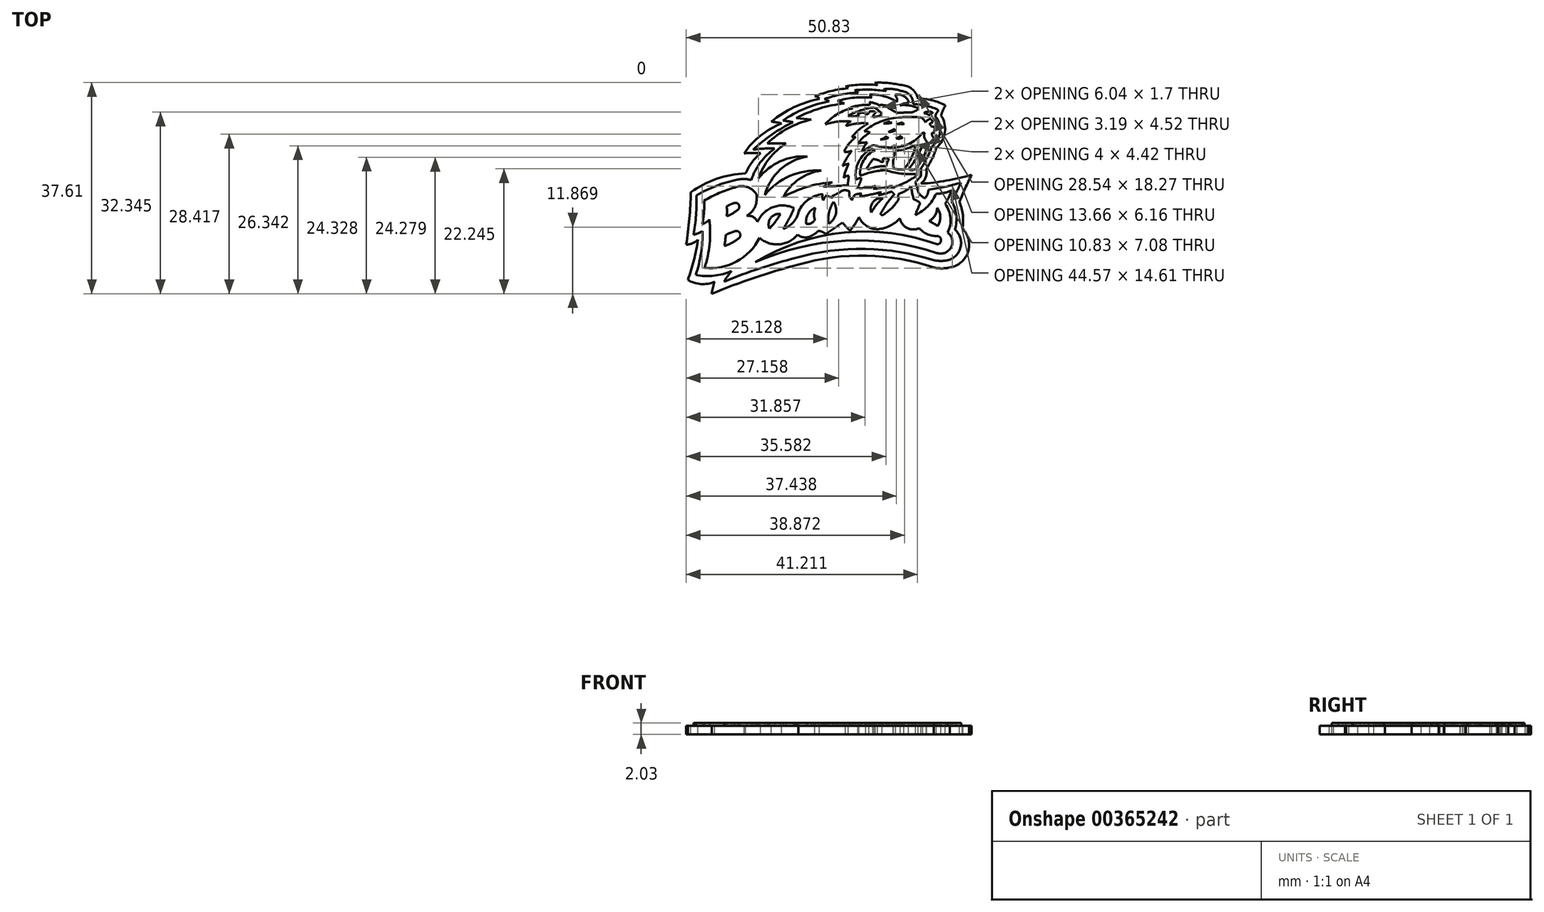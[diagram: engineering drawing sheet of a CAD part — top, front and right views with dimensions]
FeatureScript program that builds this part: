
annotation { "Feature Type Name" : "Feature", "Feature Type Description" : "" }
export const myFeature = defineFeature(function(context is Context, id is Id, definition is map)
    precondition{}
    {
        {
            var Q0;
            Q0=qCreatedBy(makeId("Top.planeOp"),FACE);
            var sketch = newSketch(context, id + "F0", { "sketchPlane" : qUnion([Q0])});
            skLineSegment(sketch, "E0", {"start": v(-9.68, 4.6) * mm, "end": v(-12.98, 4.6) * mm});
            skLineSegment(sketch, "E1", {"start": v(-7.81, 9.13) * mm, "end": v(-5.14, 8.87) * mm});
            skLineSegment(sketch, "E2", {"start": v(-0.46, 12.2) * mm, "end": v(0.77, 11.72) * mm});
            skLineSegment(sketch, "E3", {"start": v(5.28, 13.32) * mm, "end": v(5.62, 12.76) * mm});
            skArc(sketch, "E4", {"start": v(10.1, 12.03) * mm, "mid": v(7.78, 13.04) * mm, "end": v(5.28, 13.32) * mm});
            skArc(sketch, "E5", {"start": v(5.62, 12.76) * mm, "mid": v(2.55, 12.78) * mm, "end": v(-0.46, 12.2) * mm});
            skArc(sketch, "E6", {"start": v(0.77, 11.72) * mm, "mid": v(-3.65, 10.85) * mm, "end": v(-7.81, 9.13) * mm});
            skArc(sketch, "E7", {"start": v(-5.14, 8.87) * mm, "mid": v(-9.36, 7.3) * mm, "end": v(-12.98, 4.6) * mm});
            skArc(sketch, "E8", {"start": v(-9.68, 4.6) * mm, "mid": v(-12.64, 1.92) * mm, "end": v(-14.53, -1.6) * mm});
            skArc(sketch, "E9", {"start": v(-5.85, 2.3) * mm, "mid": v(-10.68, 1.43) * mm, "end": v(-14.53, -1.6) * mm});
            skArc(sketch, "E10", {"start": v(-5.85, 2.3) * mm, "mid": v(-10.66, -0.03) * mm, "end": v(-13.45, -4.58) * mm});
            skArc(sketch, "E11", {"start": v(-3.37, -0.22) * mm, "mid": v(-8.94, -1.17) * mm, "end": v(-13.45, -4.58) * mm});
            skArc(sketch, "E12", {"start": v(-3.37, -0.22) * mm, "mid": v(-7.34, -1.75) * mm, "end": v(-10.14, -4.94) * mm});
            skArc(sketch, "E13", {"start": v(-1.42, -2.32) * mm, "mid": v(-5.93, -3.13) * mm, "end": v(-10.14, -4.94) * mm});
            skArc(sketch, "E14", {"start": v(-1.42, -2.32) * mm, "mid": v(-2.2, -2.67) * mm, "end": v(-2.98, -3.05) * mm});
            skArc(sketch, "E15", {"start": v(-2.98, -3.05) * mm, "mid": v(-0.82, -2.97) * mm, "end": v(1.35, -2.86) * mm});
            skArc(sketch, "E16", {"start": v(1.55, -1.16) * mm, "mid": v(1.44, -2) * mm, "end": v(1.35, -2.86) * mm});
            skArc(sketch, "E17", {"start": v(1.55, -1.16) * mm, "mid": v(1.07, -1.21) * mm, "end": v(0.68, -1.5) * mm});
            skArc(sketch, "E18", {"start": v(1.55, 1.01) * mm, "mid": v(0.98, -0.2) * mm, "end": v(0.68, -1.5) * mm});
            skArc(sketch, "E19", {"start": v(1.55, 1.01) * mm, "mid": v(0.97, 0.86) * mm, "end": v(0.44, 0.6) * mm});
            skArc(sketch, "E20", {"start": v(2.1, 3.35) * mm, "mid": v(1.2, 2.02) * mm, "end": v(0.44, 0.6) * mm});
            skArc(sketch, "E21", {"start": v(0.68, 3.16) * mm, "mid": v(1.4, 3.13) * mm, "end": v(2.1, 3.35) * mm});
            skArc(sketch, "E22", {"start": v(2.8, 5.75) * mm, "mid": v(1.6, 4.58) * mm, "end": v(0.68, 3.16) * mm});
            skArc(sketch, "E23", {"start": v(2.8, 5.75) * mm, "mid": v(2.45, 5.77) * mm, "end": v(2.1, 5.75) * mm});
            skArc(sketch, "E24", {"start": v(4.98, 8.2) * mm, "mid": v(3.41, 7.12) * mm, "end": v(2.1, 5.75) * mm});
            skArc(sketch, "E25", {"start": v(4.98, 8.2) * mm, "mid": v(3, 8.16) * mm, "end": v(1.05, 7.73) * mm});
            skArc(sketch, "E26", {"start": v(1.94, 8.53) * mm, "mid": v(1.4, 8.23) * mm, "end": v(1.05, 7.73) * mm});
            skArc(sketch, "E27", {"start": v(1.94, 8.53) * mm, "mid": v(-0.37, 8.53) * mm, "end": v(-2.64, 8.02) * mm});
            skArc(sketch, "E28", {"start": v(2.29, 10.88) * mm, "mid": v(-0.43, 9.9) * mm, "end": v(-2.64, 8.02) * mm});
            skArc(sketch, "E29", {"start": v(2.29, 10.88) * mm, "mid": v(2.09, 10.98) * mm, "end": v(1.88, 11.07) * mm});
            skArc(sketch, "E30", {"start": v(5.25, 11.51) * mm, "mid": v(3.55, 11.41) * mm, "end": v(1.88, 11.07) * mm});
            skArc(sketch, "E31", {"start": v(5.25, 11.51) * mm, "mid": v(5.3, 11.75) * mm, "end": v(5.25, 11.98) * mm});
            skArc(sketch, "E32", {"start": v(6.95, 11.43) * mm, "mid": v(6.13, 11.8) * mm, "end": v(5.25, 11.98) * mm});
            skArc(sketch, "E33", {"start": v(8.33, 11.35) * mm, "mid": v(7.64, 11.45) * mm, "end": v(6.95, 11.43) * mm});
            skArc(sketch, "E34", {"start": v(8.55, 10.96) * mm, "mid": v(8.5, 11.2) * mm, "end": v(8.33, 11.35) * mm});
            skArc(sketch, "E35", {"start": v(8.55, 10.96) * mm, "mid": v(9.41, 10.45) * mm, "end": v(10.33, 10.05) * mm});
            skArc(sketch, "E36", {"start": v(12.82, 10.15) * mm, "mid": v(11.58, 10.13) * mm, "end": v(10.33, 10.05) * mm});
            skArc(sketch, "E37", {"start": v(12.82, 10.15) * mm, "mid": v(13.46, 10.44) * mm, "end": v(14, 10.88) * mm});
            skArc(sketch, "E38", {"start": v(14, 10.88) * mm, "mid": v(12.37, 11.37) * mm, "end": v(10.67, 11.43) * mm});
            skArc(sketch, "E39", {"start": v(12.27, 11.86) * mm, "mid": v(11.45, 11.74) * mm, "end": v(10.67, 11.43) * mm});
            skArc(sketch, "E40", {"start": v(10.1, 12.03) * mm, "mid": v(10.1, 12.7) * mm, "end": v(9.75, 13.25) * mm});
            skArc(sketch, "E41", {"start": v(12.27, 11.86) * mm, "mid": v(11.3, 13.08) * mm, "end": v(9.75, 13.25) * mm});
            skArc(sketch, "E42", {"start": v(16.51, 10.14) * mm, "mid": v(15.71, 10.28) * mm, "end": v(14.93, 10.05) * mm});
            skArc(sketch, "E43", {"start": v(16.17, 9.93) * mm, "mid": v(16.36, 10) * mm, "end": v(16.51, 10.14) * mm});
            skArc(sketch, "E44", {"start": v(15.52, 9.9) * mm, "mid": v(15.85, 9.7) * mm, "end": v(16.17, 9.93) * mm});
            skArc(sketch, "E45", {"start": v(14.93, 10.05) * mm, "mid": v(15.22, 9.95) * mm, "end": v(15.52, 9.9) * mm});
            skArc(sketch, "E46", {"start": v(6.07, 11.05) * mm, "mid": v(3.67, 10.5) * mm, "end": v(1.42, 9.55) * mm});
            skArc(sketch, "E47", {"start": v(7.46, 9.83) * mm, "mid": v(6.81, 10.5) * mm, "end": v(6.07, 11.05) * mm});
            skArc(sketch, "E48", {"start": v(5.83, 9.35) * mm, "mid": v(6.7, 9.44) * mm, "end": v(7.46, 9.83) * mm});
            skArc(sketch, "E49", {"start": v(6.3, 10.05) * mm, "mid": v(6, 9.74) * mm, "end": v(5.83, 9.35) * mm});
            skArc(sketch, "E50", {"start": v(6.3, 10.05) * mm, "mid": v(6.26, 10.17) * mm, "end": v(6.18, 10.26) * mm});
            skArc(sketch, "E51", {"start": v(6.18, 10.26) * mm, "mid": v(5.66, 10.36) * mm, "end": v(5.14, 10.26) * mm});
            skArc(sketch, "E52", {"start": v(4.58, 9.85) * mm, "mid": v(4.98, 9.89) * mm, "end": v(5.14, 10.26) * mm});
            skArc(sketch, "E53", {"start": v(4.58, 9.85) * mm, "mid": v(4.31, 10.05) * mm, "end": v(3.98, 10.11) * mm});
            skArc(sketch, "E54", {"start": v(3.98, 10.11) * mm, "mid": v(3.54, 10.03) * mm, "end": v(3.14, 9.85) * mm});
            skArc(sketch, "E55", {"start": v(3.35, 9.58) * mm, "mid": v(3.26, 9.72) * mm, "end": v(3.14, 9.85) * mm});
            skArc(sketch, "E56", {"start": v(1.42, 9.55) * mm, "mid": v(2.38, 9.47) * mm, "end": v(3.35, 9.58) * mm});
            skArc(sketch, "E57", {"start": v(10.38, 9.25) * mm, "mid": v(7.14, 8.5) * mm, "end": v(4.28, 6.8) * mm});
            skArc(sketch, "E58", {"start": v(14.46, 9.25) * mm, "mid": v(12.42, 9.35) * mm, "end": v(10.38, 9.25) * mm});
            skArc(sketch, "E59", {"start": v(15.21, 8.4) * mm, "mid": v(14.88, 8.86) * mm, "end": v(14.46, 9.25) * mm});
            skArc(sketch, "E60", {"start": v(16.06, 9.01) * mm, "mid": v(15.59, 8.77) * mm, "end": v(15.21, 8.4) * mm});
            skArc(sketch, "E61", {"start": v(16.54, 8.4) * mm, "mid": v(16.35, 8.74) * mm, "end": v(16.06, 9.01) * mm});
            skArc(sketch, "E62", {"start": v(16.54, 8.4) * mm, "mid": v(16.21, 8.27) * mm, "end": v(15.92, 8.08) * mm});
            skArc(sketch, "E63", {"start": v(16.29, 7.63) * mm, "mid": v(16.12, 7.87) * mm, "end": v(15.92, 8.08) * mm});
            skArc(sketch, "E64", {"start": v(16.8, 7.55) * mm, "mid": v(16.55, 7.62) * mm, "end": v(16.29, 7.63) * mm});
            skArc(sketch, "E65", {"start": v(16.71, 6.51) * mm, "mid": v(16.84, 7.03) * mm, "end": v(16.8, 7.55) * mm});
            skArc(sketch, "E66", {"start": v(16.38, 6.52) * mm, "mid": v(16.55, 6.5) * mm, "end": v(16.71, 6.51) * mm});
            skArc(sketch, "E67", {"start": v(16.38, 6.52) * mm, "mid": v(16.39, 6.2) * mm, "end": v(16.43, 5.9) * mm});
            skArc(sketch, "E68", {"start": v(16.8, 5.4) * mm, "mid": v(16.65, 5.68) * mm, "end": v(16.43, 5.9) * mm});
            skArc(sketch, "E69", {"start": v(15.82, 4.56) * mm, "mid": v(16.37, 4.92) * mm, "end": v(16.8, 5.4) * mm});
            skArc(sketch, "E70", {"start": v(14.95, 6.1) * mm, "mid": v(15.2, 5.23) * mm, "end": v(15.82, 4.56) * mm});
            skArc(sketch, "E71", {"start": v(15.03, 6.33) * mm, "mid": v(14.95, 6.24) * mm, "end": v(14.95, 6.1) * mm});
            skArc(sketch, "E72", {"start": v(15.03, 6.33) * mm, "mid": v(15.02, 6.48) * mm, "end": v(14.88, 6.51) * mm});
            skArc(sketch, "E73", {"start": v(14.88, 6.51) * mm, "mid": v(14.73, 6.48) * mm, "end": v(14.61, 6.38) * mm});
            skArc(sketch, "E74", {"start": v(9.25, 3.89) * mm, "mid": v(12.22, 4.51) * mm, "end": v(14.61, 6.38) * mm});
            skArc(sketch, "E75", {"start": v(5.98, 4.3) * mm, "mid": v(7.6, 3.98) * mm, "end": v(9.25, 3.89) * mm});
            skArc(sketch, "E76", {"start": v(5.98, 4.3) * mm, "mid": v(5.63, 4.2) * mm, "end": v(5.3, 4.04) * mm});
            skArc(sketch, "E77", {"start": v(3.85, 3.19) * mm, "mid": v(4.59, 3.6) * mm, "end": v(5.3, 4.04) * mm});
            skArc(sketch, "E78", {"start": v(4.81, 4.79) * mm, "mid": v(4.27, 4.02) * mm, "end": v(3.85, 3.19) * mm});
            skArc(sketch, "E79", {"start": v(4.81, 4.79) * mm, "mid": v(4, 4.75) * mm, "end": v(3.19, 4.62) * mm});
            skArc(sketch, "E80", {"start": v(5.3, 6.55) * mm, "mid": v(4.13, 5.7) * mm, "end": v(3.19, 4.62) * mm});
            skArc(sketch, "E81", {"start": v(5.3, 6.55) * mm, "mid": v(4.81, 6.76) * mm, "end": v(4.28, 6.8) * mm});
            skArc(sketch, "E82", {"start": v(7.73, 8.16) * mm, "mid": v(8.25, 8.34) * mm, "end": v(8.74, 8.56) * mm});
            skArc(sketch, "E83", {"start": v(8.74, 8.56) * mm, "mid": v(8.94, 8.35) * mm, "end": v(9.23, 8.31) * mm});
            skArc(sketch, "E84", {"start": v(7.73, 8.16) * mm, "mid": v(8.49, 8.18) * mm, "end": v(9.23, 8.31) * mm});
            skArc(sketch, "E85", {"start": v(10.14, 8.12) * mm, "mid": v(10.6, 8.2) * mm, "end": v(11.03, 8.42) * mm});
            skArc(sketch, "E86", {"start": v(11.03, 8.42) * mm, "mid": v(11.18, 8.22) * mm, "end": v(11.42, 8.12) * mm});
            skArc(sketch, "E87", {"start": v(10.14, 8.12) * mm, "mid": v(10.78, 8.02) * mm, "end": v(11.42, 8.12) * mm});
            skArc(sketch, "E88", {"start": v(7.17, 5.33) * mm, "mid": v(7.9, 5.4) * mm, "end": v(8.6, 5.6) * mm});
            skArc(sketch, "E89", {"start": v(8.17, 5.86) * mm, "mid": v(8.38, 5.72) * mm, "end": v(8.6, 5.6) * mm});
            skArc(sketch, "E90", {"start": v(7.17, 5.33) * mm, "mid": v(7.72, 5.51) * mm, "end": v(8.17, 5.86) * mm});
            skArc(sketch, "E91", {"start": v(9.96, 5.53) * mm, "mid": v(10.4, 5.7) * mm, "end": v(10.77, 5.98) * mm});
            skArc(sketch, "E92", {"start": v(10.77, 5.98) * mm, "mid": v(10.9, 5.75) * mm, "end": v(11.15, 5.66) * mm});
            skArc(sketch, "E93", {"start": v(9.96, 5.53) * mm, "mid": v(10.57, 5.48) * mm, "end": v(11.15, 5.66) * mm});
            skArc(sketch, "E94", {"start": v(8.6, 6.68) * mm, "mid": v(9.14, 6.93) * mm, "end": v(9.65, 7.2) * mm});
            skArc(sketch, "E95", {"start": v(9.65, 7.2) * mm, "mid": v(9.74, 7.05) * mm, "end": v(9.88, 6.95) * mm});
            skArc(sketch, "E96", {"start": v(8.6, 6.68) * mm, "mid": v(9.26, 6.73) * mm, "end": v(9.88, 6.95) * mm});
            skArc(sketch, "E97", {"start": v(5.52, 3.63) * mm, "mid": v(3.3, 1.34) * mm, "end": v(2.8, -1.81) * mm});
            skArc(sketch, "E98", {"start": v(3.7, -1.49) * mm, "mid": v(3.25, -1.64) * mm, "end": v(2.8, -1.81) * mm});
            skArc(sketch, "E99", {"start": v(3.64, -2.08) * mm, "mid": v(3.72, -1.79) * mm, "end": v(3.7, -1.49) * mm});
            skArc(sketch, "E100", {"start": v(3.08, -3.32) * mm, "mid": v(3.39, -2.71) * mm, "end": v(3.64, -2.08) * mm});
            skArc(sketch, "E101", {"start": v(3.08, -3.32) * mm, "mid": v(4.74, -3.29) * mm, "end": v(6.35, -2.9) * mm});
            skArc(sketch, "E102", {"start": v(5.9, -3.45) * mm, "mid": v(6.2, -3.23) * mm, "end": v(6.35, -2.9) * mm});
            skArc(sketch, "E103", {"start": v(5.9, -3.45) * mm, "mid": v(7.63, -3.3) * mm, "end": v(9.31, -2.9) * mm});
            skArc(sketch, "E104", {"start": v(9.1, -3.27) * mm, "mid": v(9.24, -3.1) * mm, "end": v(9.31, -2.9) * mm});
            skArc(sketch, "E105", {"start": v(9.1, -3.27) * mm, "mid": v(11.43, -2.43) * mm, "end": v(13.54, -1.16) * mm});
            skArc(sketch, "E106", {"start": v(13.54, -1.16) * mm, "mid": v(13.58, -1) * mm, "end": v(13.54, -0.84) * mm});
            skArc(sketch, "E107", {"start": v(8.15, -0.14) * mm, "mid": v(10.81, -0.75) * mm, "end": v(13.54, -0.84) * mm});
            skArc(sketch, "E108", {"start": v(8.15, -0.14) * mm, "mid": v(5.82, -0.44) * mm, "end": v(3.58, -1.16) * mm});
            skArc(sketch, "E109", {"start": v(6.23, 3.41) * mm, "mid": v(4.15, 1.56) * mm, "end": v(3.58, -1.16) * mm});
            skArc(sketch, "E110", {"start": v(6.23, 3.41) * mm, "mid": v(5.89, 3.57) * mm, "end": v(5.52, 3.63) * mm});
            skArc(sketch, "E111", {"start": v(4.7, 0.16) * mm, "mid": v(5.28, 0.98) * mm, "end": v(5.8, 1.83) * mm});
            skArc(sketch, "E112", {"start": v(4.93, 0) * mm, "mid": v(4.86, 0.15) * mm, "end": v(4.7, 0.16) * mm});
            skArc(sketch, "E113", {"start": v(8.24, 0.59) * mm, "mid": v(6.56, 0.46) * mm, "end": v(4.93, 0) * mm});
            skArc(sketch, "E114", {"start": v(8.6, 1.67) * mm, "mid": v(8.37, 1.15) * mm, "end": v(8.24, 0.59) * mm});
            skArc(sketch, "E115", {"start": v(8.6, 1.67) * mm, "mid": v(8.6, 1.81) * mm, "end": v(8.55, 1.94) * mm});
            skArc(sketch, "E116", {"start": v(8.55, 1.94) * mm, "mid": v(8.1, 1.96) * mm, "end": v(7.66, 1.92) * mm});
            skArc(sketch, "E117", {"start": v(7.66, 1.92) * mm, "mid": v(7.63, 1.7) * mm, "end": v(7.7, 1.47) * mm});
            skArc(sketch, "E118", {"start": v(7.33, 1.33) * mm, "mid": v(7.55, 1.31) * mm, "end": v(7.7, 1.47) * mm});
            skArc(sketch, "E119", {"start": v(7.33, 1.33) * mm, "mid": v(6.6, 1.7) * mm, "end": v(5.8, 1.83) * mm});
            skArc(sketch, "E120", {"start": v(9.88, 3.3) * mm, "mid": v(11.73, 3.65) * mm, "end": v(13.45, 4.39) * mm});
            skArc(sketch, "E121", {"start": v(11.33, 0) * mm, "mid": v(12.7, 2.04) * mm, "end": v(13.45, 4.39) * mm});
            skArc(sketch, "E122", {"start": v(9.52, 0.16) * mm, "mid": v(10.42, -0.02) * mm, "end": v(11.33, 0) * mm});
            skArc(sketch, "E123", {"start": v(9.88, 3.3) * mm, "mid": v(9.5, 1.76) * mm, "end": v(9.52, 0.16) * mm});
            skArc(sketch, "E124", {"start": v(12.2, 0) * mm, "mid": v(13.62, 2.1) * mm, "end": v(14.72, 4.39) * mm});
            skArc(sketch, "E125", {"start": v(15.39, 3.63) * mm, "mid": v(15.11, 4.06) * mm, "end": v(14.72, 4.39) * mm});
            skArc(sketch, "E126", {"start": v(13.45, 0.07) * mm, "mid": v(14.61, 1.75) * mm, "end": v(15.39, 3.63) * mm});
            skArc(sketch, "E127", {"start": v(12.2, 0) * mm, "mid": v(12.83, -0.13) * mm, "end": v(13.45, 0.07) * mm});
            skArc(sketch, "E128", {"start": v(13.02, 11.85) * mm, "mid": v(12.36, 13.32) * mm, "end": v(10.87, 13.95) * mm});
            skArc(sketch, "E129", {"start": v(10.87, 13.95) * mm, "mid": v(9.33, 14.32) * mm, "end": v(7.74, 14.28) * mm});
            skArc(sketch, "E130", {"start": v(8.16, 13.95) * mm, "mid": v(7.98, 14.16) * mm, "end": v(7.74, 14.28) * mm});
            skArc(sketch, "E131", {"start": v(8.16, 13.95) * mm, "mid": v(5.37, 14.2) * mm, "end": v(2.56, 14.1) * mm});
            skArc(sketch, "E132", {"start": v(3.2, 13.67) * mm, "mid": v(2.91, 13.93) * mm, "end": v(2.56, 14.1) * mm});
            skArc(sketch, "E133", {"start": v(3.2, 13.67) * mm, "mid": v(0.16, 13.34) * mm, "end": v(-2.78, 12.53) * mm});
            skArc(sketch, "E134", {"start": v(-1.98, 12.13) * mm, "mid": v(-2.37, 12.36) * mm, "end": v(-2.78, 12.53) * mm});
            skArc(sketch, "E135", {"start": v(-1.98, 12.13) * mm, "mid": v(-6.26, 10.84) * mm, "end": v(-10.2, 8.72) * mm});
            skArc(sketch, "E136", {"start": v(-8.38, 8.4) * mm, "mid": v(-9.3, 8.57) * mm, "end": v(-10.2, 8.72) * mm});
            skArc(sketch, "E137", {"start": v(-8.38, 8.4) * mm, "mid": v(-12.13, 6.22) * mm, "end": v(-15.5, 3.49) * mm});
            skArc(sketch, "E138", {"start": v(-11.68, 3.7) * mm, "mid": v(-13.6, 3.7) * mm, "end": v(-15.5, 3.49) * mm});
            skArc(sketch, "E139", {"start": v(-11.68, 3.7) * mm, "mid": v(-14.21, 1.23) * mm, "end": v(-15.86, -1.9) * mm});
            skArc(sketch, "E140", {"start": v(-24.58, -9.74) * mm, "mid": v(-24.27, -7.67) * mm, "end": v(-24.25, -5.57) * mm});
            skArc(sketch, "E141", {"start": v(-24.58, -9.74) * mm, "mid": v(-23.88, -9.42) * mm, "end": v(-23.3, -8.93) * mm});
            skArc(sketch, "E142", {"start": v(-24.17, -17.55) * mm, "mid": v(-23.26, -13.28) * mm, "end": v(-23.3, -8.93) * mm});
            skArc(sketch, "E143", {"start": v(-24.17, -17.55) * mm, "mid": v(-18.43, -16.4) * mm, "end": v(-14.35, -12.2) * mm});
            skArc(sketch, "E144", {"start": v(-14.35, -12.2) * mm, "mid": v(-10.86, -13.35) * mm, "end": v(-7.61, -11.64) * mm});
            skArc(sketch, "E145", {"start": v(-7.61, -11.64) * mm, "mid": v(-6.2, -12.12) * mm, "end": v(-4.78, -11.64) * mm});
            skArc(sketch, "E146", {"start": v(-4.78, -11.64) * mm, "mid": v(-4.29, -11.32) * mm, "end": v(-3.85, -10.94) * mm});
            skArc(sketch, "E147", {"start": v(-2.55, -11.5) * mm, "mid": v(-3.17, -11.15) * mm, "end": v(-3.85, -10.94) * mm});
            skArc(sketch, "E148", {"start": v(-2.55, -11.5) * mm, "mid": v(-1.05, -10.5) * mm, "end": v(0.45, -9.5) * mm});
            skArc(sketch, "E149", {"start": v(0.45, -9.5) * mm, "mid": v(1.07, -10.24) * mm, "end": v(1.74, -10.94) * mm});
            skArc(sketch, "E150", {"start": v(1.74, -10.94) * mm, "mid": v(2.64, -9.77) * mm, "end": v(3.37, -8.49) * mm});
            skArc(sketch, "E151", {"start": v(3.37, -8.49) * mm, "mid": v(4.6, -10) * mm, "end": v(6.43, -10.67) * mm});
            skArc(sketch, "E152", {"start": v(6.43, -10.67) * mm, "mid": v(8.75, -10.13) * mm, "end": v(10.65, -8.7) * mm});
            skArc(sketch, "E153", {"start": v(10.65, -8.7) * mm, "mid": v(11.92, -10.44) * mm, "end": v(14.08, -10.47) * mm});
            skArc(sketch, "E154", {"start": v(14.08, -10.47) * mm, "mid": v(15.54, -11.55) * mm, "end": v(17.34, -11.86) * mm});
            skArc(sketch, "E155", {"start": v(17.34, -13.36) * mm, "mid": v(17.98, -12.6) * mm, "end": v(17.34, -11.86) * mm});
            skArc(sketch, "E156", {"start": v(17.34, -13.36) * mm, "mid": v(0.74, -11.26) * mm, "end": v(-15.14, -16.54) * mm});
            skArc(sketch, "E157", {"start": v(17.28, -14.9) * mm, "mid": v(0.92, -12.72) * mm, "end": v(-15.14, -16.54) * mm});
            skArc(sketch, "E158", {"start": v(17.28, -14.9) * mm, "mid": v(19.78, -13.86) * mm, "end": v(19.16, -11.23) * mm});
            skArc(sketch, "E159", {"start": v(19.16, -11.23) * mm, "mid": v(19.65, -8.63) * mm, "end": v(18.7, -6.17) * mm});
            skArc(sketch, "E160", {"start": v(17.07, -4.37) * mm, "mid": v(17.1, -4.36) * mm, "end": v(17.13, -4.36) * mm});
            skArc(sketch, "E161", {"start": v(13.39, -8.11) * mm, "mid": v(15.58, -6.59) * mm, "end": v(17.07, -4.37) * mm});
            skArc(sketch, "E162", {"start": v(13.39, -8.11) * mm, "mid": v(13.82, -7.08) * mm, "end": v(14.23, -6.03) * mm});
            skArc(sketch, "E163", {"start": v(14.23, -6.03) * mm, "mid": v(13.74, -5.6) * mm, "end": v(13.13, -5.37) * mm});
            skArc(sketch, "E164", {"start": v(12.66, -3.05) * mm, "mid": v(12.84, -4.22) * mm, "end": v(13.13, -5.37) * mm});
            skArc(sketch, "E165", {"start": v(10.39, -4.36) * mm, "mid": v(11.6, -3.85) * mm, "end": v(12.66, -3.05) * mm});
            skArc(sketch, "E166", {"start": v(10.39, -4.36) * mm, "mid": v(10.36, -4.86) * mm, "end": v(10.39, -5.37) * mm});
            skArc(sketch, "E167", {"start": v(7.66, -8.11) * mm, "mid": v(9.19, -6.9) * mm, "end": v(10.39, -5.37) * mm});
            skArc(sketch, "E168", {"start": v(7.37, -7.66) * mm, "mid": v(7.28, -8.04) * mm, "end": v(7.66, -8.11) * mm});
            skArc(sketch, "E169", {"start": v(9.64, -4.5) * mm, "mid": v(8.39, -6) * mm, "end": v(7.37, -7.66) * mm});
            skArc(sketch, "E170", {"start": v(9.64, -4.5) * mm, "mid": v(9.43, -4.21) * mm, "end": v(9.16, -3.97) * mm});
            skArc(sketch, "E171", {"start": v(6.85, -4.6) * mm, "mid": v(8.01, -4.32) * mm, "end": v(9.16, -3.97) * mm});
            skArc(sketch, "E172", {"start": v(7.37, -4.05) * mm, "mid": v(7.07, -4.3) * mm, "end": v(6.85, -4.6) * mm});
            skArc(sketch, "E173", {"start": v(3.6, -4.84) * mm, "mid": v(5.5, -4.48) * mm, "end": v(7.37, -4.05) * mm});
            skArc(sketch, "E174", {"start": v(3.82, -4.37) * mm, "mid": v(3.66, -4.58) * mm, "end": v(3.6, -4.84) * mm});
            skArc(sketch, "E175", {"start": v(3.82, -4.37) * mm, "mid": v(3.27, -4.36) * mm, "end": v(2.73, -4.5) * mm});
            skArc(sketch, "E176", {"start": v(2.73, -4.5) * mm, "mid": v(2.32, -4.94) * mm, "end": v(2.15, -5.5) * mm});
            skArc(sketch, "E177", {"start": v(1.65, -3.97) * mm, "mid": v(1.68, -4.8) * mm, "end": v(2.15, -5.5) * mm});
            skArc(sketch, "E178", {"start": v(1.65, -3.97) * mm, "mid": v(0.81, -3.7) * mm, "end": v(0, -4.05) * mm});
            skArc(sketch, "E179", {"start": v(-1.39, -4.73) * mm, "mid": v(-0.68, -4.41) * mm, "end": v(0, -4.05) * mm});
            skArc(sketch, "E180", {"start": v(-1.39, -5.02) * mm, "mid": v(-1.36, -4.87) * mm, "end": v(-1.39, -4.73) * mm});
            skArc(sketch, "E181", {"start": v(-2.42, -4.6) * mm, "mid": v(-1.93, -4.87) * mm, "end": v(-1.39, -5.02) * mm});
            skArc(sketch, "E182", {"start": v(-2.42, -4.6) * mm, "mid": v(-2.77, -5.05) * mm, "end": v(-3, -5.56) * mm});
            skArc(sketch, "E183", {"start": v(-3.1, -4.43) * mm, "mid": v(-3.16, -5) * mm, "end": v(-3, -5.56) * mm});
            skArc(sketch, "E184", {"start": v(-3.1, -4.43) * mm, "mid": v(-5.64, -5.37) * mm, "end": v(-7.38, -7.45) * mm});
            skArc(sketch, "E185", {"start": v(-10.1, -10.6) * mm, "mid": v(-8.33, -9.38) * mm, "end": v(-7.38, -7.45) * mm});
            skArc(sketch, "E186", {"start": v(-10.1, -10.6) * mm, "mid": v(-9.1, -8.79) * mm, "end": v(-8.2, -6.91) * mm});
            skArc(sketch, "E187", {"start": v(-8.2, -6.91) * mm, "mid": v(-11.98, -6.74) * mm, "end": v(-14.72, -9.36) * mm});
            skArc(sketch, "E188", {"start": v(-14.72, -9.36) * mm, "mid": v(-15.51, -8.48) * mm, "end": v(-16.68, -8.3) * mm});
            skArc(sketch, "E189", {"start": v(-16.68, -8.3) * mm, "mid": v(-15.15, -6.62) * mm, "end": v(-14.95, -4.36) * mm});
            skArc(sketch, "E190", {"start": v(-14.95, -4.36) * mm, "mid": v(-16.66, -3.1) * mm, "end": v(-18.77, -3.22) * mm});
            skArc(sketch, "E191", {"start": v(-18.77, -3.22) * mm, "mid": v(-21.58, -4.23) * mm, "end": v(-24.25, -5.57) * mm});
            skArc(sketch, "E192", {"start": v(-18.29, -7.24) * mm, "mid": v(-18.03, -6.33) * mm, "end": v(-18.92, -6.02) * mm});
            skArc(sketch, "E193", {"start": v(-18.1, -12.31) * mm, "mid": v(-17.86, -11.37) * mm, "end": v(-18.78, -11.03) * mm});
            skArc(sketch, "E194", {"start": v(-18.78, -11.03) * mm, "mid": v(-19.6, -11.32) * mm, "end": v(-20.38, -11.68) * mm});
            skArc(sketch, "E195", {"start": v(-20.64, -13.62) * mm, "mid": v(-20.48, -12.65) * mm, "end": v(-20.38, -11.68) * mm});
            skArc(sketch, "E196", {"start": v(-20.64, -13.62) * mm, "mid": v(-19.3, -13.1) * mm, "end": v(-18.1, -12.31) * mm});
            skArc(sketch, "E197", {"start": v(-20.22, -8.34) * mm, "mid": v(-19.21, -7.87) * mm, "end": v(-18.29, -7.24) * mm});
            skArc(sketch, "E198", {"start": v(-20.22, -8.34) * mm, "mid": v(-20.16, -7.47) * mm, "end": v(-20.22, -6.61) * mm});
            skArc(sketch, "E199", {"start": v(-18.92, -6.02) * mm, "mid": v(-19.6, -6.27) * mm, "end": v(-20.22, -6.61) * mm});
            skArc(sketch, "E200", {"start": v(-10.64, -7.94) * mm, "mid": v(-12.38, -8.67) * mm, "end": v(-12.6, -10.54) * mm});
            skArc(sketch, "E201", {"start": v(-12.6, -10.54) * mm, "mid": v(-11.54, -9.3) * mm, "end": v(-10.64, -7.94) * mm});
            skArc(sketch, "E202", {"start": v(-4.4, -6.86) * mm, "mid": v(-5.75, -7.98) * mm, "end": v(-6.04, -9.7) * mm});
            skArc(sketch, "E203", {"start": v(-4.4, -6.86) * mm, "mid": v(-4.64, -7.92) * mm, "end": v(-4.52, -9) * mm});
            skArc(sketch, "E204", {"start": v(-6.04, -9.7) * mm, "mid": v(-5.17, -9.59) * mm, "end": v(-4.52, -9) * mm});
            skArc(sketch, "E205", {"start": v(-1.19, -5.8) * mm, "mid": v(-1.97, -7.67) * mm, "end": v(-2.08, -9.7) * mm});
            skArc(sketch, "E206", {"start": v(-2.08, -9.7) * mm, "mid": v(-0.77, -7.95) * mm, "end": v(-1.19, -5.8) * mm});
            skArc(sketch, "E207", {"start": v(7.61, -5.11) * mm, "mid": v(5.87, -5.82) * mm, "end": v(5.56, -7.68) * mm});
            skArc(sketch, "E208", {"start": v(7.61, -5.11) * mm, "mid": v(6.48, -6.3) * mm, "end": v(5.56, -7.68) * mm});
            skArc(sketch, "E209", {"start": v(15.87, -9.22) * mm, "mid": v(16.89, -8.22) * mm, "end": v(17.3, -6.86) * mm});
            skArc(sketch, "E210", {"start": v(17.4, -10.1) * mm, "mid": v(16.65, -9.63) * mm, "end": v(15.87, -9.22) * mm});
            skArc(sketch, "E211", {"start": v(17.4, -10.1) * mm, "mid": v(17.84, -8.46) * mm, "end": v(17.3, -6.86) * mm});
            skArc(sketch, "E212", {"start": v(17.07, -4.37) * mm, "mid": v(18.49, -4.19) * mm, "end": v(19.85, -3.77) * mm});
            skArc(sketch, "E213", {"start": v(18.7, -6.17) * mm, "mid": v(19.35, -5) * mm, "end": v(19.85, -3.77) * mm});
            skArc(sketch, "E214", {"start": v(13.02, 11.85) * mm, "mid": v(13.04, 11.74) * mm, "end": v(13.06, 11.63) * mm});
            skArc(sketch, "E215", {"start": v(17.29, 10.7) * mm, "mid": v(15.22, 11.35) * mm, "end": v(13.06, 11.63) * mm});
            skArc(sketch, "E216", {"start": v(17.33, 10.26) * mm, "mid": v(17.44, 10.49) * mm, "end": v(17.29, 10.7) * mm});
            skArc(sketch, "E217", {"start": v(17.33, 10.26) * mm, "mid": v(17.12, 9.92) * mm, "end": v(17, 9.53) * mm});
            skArc(sketch, "E218", {"start": v(17, 9.53) * mm, "mid": v(17.04, 9.33) * mm, "end": v(17.18, 9.17) * mm});
            skArc(sketch, "E219", {"start": v(17.77, 6.48) * mm, "mid": v(17.7, 7.88) * mm, "end": v(17.18, 9.17) * mm});
            skArc(sketch, "E220", {"start": v(16.33, 4.1) * mm, "mid": v(17.29, 5.15) * mm, "end": v(17.77, 6.48) * mm});
            skArc(sketch, "E221", {"start": v(14.4, 0.14) * mm, "mid": v(15.5, 2.06) * mm, "end": v(16.33, 4.1) * mm});
            skArc(sketch, "E222", {"start": v(14.4, -1.22) * mm, "mid": v(14.4, -0.54) * mm, "end": v(14.4, 0.14) * mm});
            skArc(sketch, "E223", {"start": v(14.4, -1.22) * mm, "mid": v(13.9, -1.76) * mm, "end": v(13.4, -2.31) * mm});
            skArc(sketch, "E224", {"start": v(13.4, -2.31) * mm, "mid": v(13.71, -3.32) * mm, "end": v(14.03, -4.34) * mm});
            skArc(sketch, "E225", {"start": v(14.03, -4.34) * mm, "mid": v(14.47, -4.72) * mm, "end": v(14.93, -5.07) * mm});
            skArc(sketch, "E226", {"start": v(14.93, -5.07) * mm, "mid": v(15.07, -5.1) * mm, "end": v(15.2, -5.07) * mm});
            skArc(sketch, "E227", {"start": v(15.2, -5.07) * mm, "mid": v(15.59, -4.37) * mm, "end": v(15.75, -3.6) * mm});
            skArc(sketch, "E228", {"start": v(15.75, -3.6) * mm, "mid": v(18.66, -3.11) * mm, "end": v(21.51, -2.36) * mm});
            skArc(sketch, "E229", {"start": v(19.87, -5.7) * mm, "mid": v(20.74, -4.05) * mm, "end": v(21.51, -2.36) * mm});
            skArc(sketch, "E230", {"start": v(20.45, -10.71) * mm, "mid": v(20.7, -8.14) * mm, "end": v(19.87, -5.7) * mm});
            skArc(sketch, "E231", {"start": v(19.16, -16.2) * mm, "mid": v(21.47, -13.85) * mm, "end": v(20.45, -10.71) * mm});
            skArc(sketch, "E232", {"start": v(16.74, -16.2) * mm, "mid": v(17.95, -16.3) * mm, "end": v(19.16, -16.2) * mm});
            skArc(sketch, "E233", {"start": v(16.74, -16.2) * mm, "mid": v(4.47, -14.17) * mm, "end": v(-7.86, -15.76) * mm});
            skArc(sketch, "E234", {"start": v(-7.86, -15.76) * mm, "mid": v(-14.34, -17.65) * mm, "end": v(-20.67, -19.99) * mm});
            skArc(sketch, "E235", {"start": v(-19.37, -18.13) * mm, "mid": v(-20.07, -19.03) * mm, "end": v(-20.67, -19.99) * mm});
            skArc(sketch, "E236", {"start": v(-25.73, -18.82) * mm, "mid": v(-22.5, -18.95) * mm, "end": v(-19.37, -18.13) * mm});
            skArc(sketch, "E237", {"start": v(-25.73, -18.82) * mm, "mid": v(-24.8, -14.96) * mm, "end": v(-24.52, -11) * mm});
            skArc(sketch, "E238", {"start": v(-26.1, -11.63) * mm, "mid": v(-25.29, -11.37) * mm, "end": v(-24.52, -11) * mm});
            skArc(sketch, "E239", {"start": v(-26.1, -11.63) * mm, "mid": v(-25.7, -8.14) * mm, "end": v(-25.59, -4.62) * mm});
            skArc(sketch, "E240", {"start": v(-18.2, -1.81) * mm, "mid": v(-22.01, -2.9) * mm, "end": v(-25.59, -4.62) * mm});
            skArc(sketch, "E241", {"start": v(-15.86, -1.9) * mm, "mid": v(-17.03, -1.71) * mm, "end": v(-18.2, -1.81) * mm});
            skArc(sketch, "E242", {"start": v(-14.16, 2.89) * mm, "mid": v(-15.64, 2.9) * mm, "end": v(-17.12, 2.87) * mm});
            skArc(sketch, "E243", {"start": v(-14.16, 2.89) * mm, "mid": v(-15.72, 1.25) * mm, "end": v(-16.86, -0.7) * mm});
            skArc(sketch, "E244", {"start": v(-16.86, -0.7) * mm, "mid": v(-21.99, -1.68) * mm, "end": v(-26.62, -4.1) * mm});
            skArc(sketch, "E245", {"start": v(-27.42, -13.43) * mm, "mid": v(-26.86, -8.78) * mm, "end": v(-26.62, -4.1) * mm});
            skArc(sketch, "E246", {"start": v(-27.42, -13.43) * mm, "mid": v(-26.3, -13.17) * mm, "end": v(-25.33, -12.54) * mm});
            skArc(sketch, "E247", {"start": v(-27.15, -19.7) * mm, "mid": v(-26.06, -16.17) * mm, "end": v(-25.33, -12.54) * mm});
            skArc(sketch, "E248", {"start": v(-27.15, -19.7) * mm, "mid": v(-24.8, -20.43) * mm, "end": v(-22.39, -20.03) * mm});
            skArc(sketch, "E249", {"start": v(-22.39, -20.03) * mm, "mid": v(-22.68, -21.08) * mm, "end": v(-22.9, -22.15) * mm});
            skArc(sketch, "E250", {"start": v(-7.43, -16.97) * mm, "mid": v(-15.25, -19.3) * mm, "end": v(-22.9, -22.15) * mm});
            skArc(sketch, "E251", {"start": v(16.66, -17.48) * mm, "mid": v(4.66, -15.37) * mm, "end": v(-7.43, -16.97) * mm});
            skArc(sketch, "E252", {"start": v(16.66, -17.48) * mm, "mid": v(18.1, -17.64) * mm, "end": v(19.54, -17.48) * mm});
            skArc(sketch, "E253", {"start": v(19.54, -17.48) * mm, "mid": v(22.8, -14.7) * mm, "end": v(21.78, -10.54) * mm});
            skArc(sketch, "E254", {"start": v(21.78, -10.54) * mm, "mid": v(21.87, -8.13) * mm, "end": v(21.25, -5.8) * mm});
            skArc(sketch, "E255", {"start": v(23.41, -0.97) * mm, "mid": v(22.29, -3.37) * mm, "end": v(21.25, -5.8) * mm});
            skArc(sketch, "E256", {"start": v(14.39, -2.56) * mm, "mid": v(18.94, -2) * mm, "end": v(23.41, -0.97) * mm});
            skArc(sketch, "E257", {"start": v(14.39, -2.56) * mm, "mid": v(15.26, -1.42) * mm, "end": v(15.33, 0) * mm});
            skArc(sketch, "E258", {"start": v(15.33, 0) * mm, "mid": v(16.38, 1.86) * mm, "end": v(17.15, 3.85) * mm});
            skArc(sketch, "E259", {"start": v(17.15, 3.85) * mm, "mid": v(18.66, 6.56) * mm, "end": v(17.98, 9.6) * mm});
            skArc(sketch, "E260", {"start": v(18.75, 11.41) * mm, "mid": v(18.32, 10.52) * mm, "end": v(17.98, 9.6) * mm});
            skArc(sketch, "E261", {"start": v(18.75, 11.41) * mm, "mid": v(16.4, 12.3) * mm, "end": v(13.9, 12.55) * mm});
            skArc(sketch, "E262", {"start": v(13.9, 12.55) * mm, "mid": v(12.76, 14.35) * mm, "end": v(10.74, 15.02) * mm});
            skArc(sketch, "E263", {"start": v(10.74, 15.02) * mm, "mid": v(8.46, 15.4) * mm, "end": v(6.14, 15.43) * mm});
            skArc(sketch, "E264", {"start": v(6.63, 15.02) * mm, "mid": v(6.43, 15.28) * mm, "end": v(6.14, 15.43) * mm});
            skArc(sketch, "E265", {"start": v(6.63, 15.02) * mm, "mid": v(3.78, 15.1) * mm, "end": v(0.94, 14.81) * mm});
            skArc(sketch, "E266", {"start": v(1.45, 14.45) * mm, "mid": v(1.22, 14.68) * mm, "end": v(0.94, 14.81) * mm});
            skArc(sketch, "E267", {"start": v(1.45, 14.45) * mm, "mid": v(-1.6, 13.97) * mm, "end": v(-4.52, 13) * mm});
            skArc(sketch, "E268", {"start": v(-3.7, 12.55) * mm, "mid": v(-4.05, 12.89) * mm, "end": v(-4.52, 13) * mm});
            skArc(sketch, "E269", {"start": v(-3.7, 12.55) * mm, "mid": v(-8.24, 11.07) * mm, "end": v(-12.25, 8.5) * mm});
            skArc(sketch, "E270", {"start": v(-10.42, 8.18) * mm, "mid": v(-11.33, 8.37) * mm, "end": v(-12.25, 8.5) * mm});
            skArc(sketch, "E271", {"start": v(-10.42, 8.18) * mm, "mid": v(-14.16, 6.02) * mm, "end": v(-17.12, 2.87) * mm});
            skLineSegment(sketch, "E272", {"start": v(-4.94, 16.73) * mm, "end": v(-17.06, 19.36) * mm});
            skSolve(sketch);
        }
        {
            var Q0;
            Q0=makeQuery(id+"F0.imprint","IMPRINT",FACE,{"disambiguationData":[TD([[makeQuery(id+"F0.imprint","IMPRINT",EDGE,{"derivedFrom":sQuery(id+"F0.wireOp",EDGE,"E128")}),-1.0]])]});
            var Q1;
            Q1=makeQuery(id+"F0.imprint","IMPRINT",FACE,{"disambiguationData":[TD([[makeQuery(id+"F0.imprint","IMPRINT",EDGE,{"derivedFrom":sQuery(id+"F0.wireOp",EDGE,"E140")}),-1.0]])]});
            var Q2;
            Q2=makeQuery(id+"F0.imprint","IMPRINT",FACE,{"disambiguationData":[TD([[makeQuery(id+"F0.imprint","IMPRINT",EDGE,{"derivedFrom":sQuery(id+"F0.wireOp",EDGE,"E0")}),-1.0]])]});
            var Q3;
            Q3=makeQuery(id+"F0.imprint","IMPRINT",FACE,{"disambiguationData":[TD([[makeQuery(id+"F0.imprint","IMPRINT",EDGE,{"derivedFrom":sQuery(id+"F0.wireOp",EDGE,"E57")}),1.0]])]});
            var Q4;
            Q4=makeQuery(id+"F0.imprint","IMPRINT",FACE,{"disambiguationData":[TD([[makeQuery(id+"F0.imprint","IMPRINT",EDGE,{"derivedFrom":sQuery(id+"F0.wireOp",EDGE,"E193")}),1.0]])]});
            var Q5;
            Q5=makeQuery(id+"F0.imprint","IMPRINT",FACE,{"disambiguationData":[TD([[makeQuery(id+"F0.imprint","IMPRINT",EDGE,{"derivedFrom":sQuery(id+"F0.wireOp",EDGE,"E192")}),1.0]])]});
            var Q6;
            Q6=makeQuery(id+"F0.imprint","IMPRINT",FACE,{"disambiguationData":[TD([[makeQuery(id+"F0.imprint","IMPRINT",EDGE,{"derivedFrom":sQuery(id+"F0.wireOp",EDGE,"E200")}),1.0]])]});
            var Q7;
            Q7=makeQuery(id+"F0.imprint","IMPRINT",FACE,{"disambiguationData":[TD([[makeQuery(id+"F0.imprint","IMPRINT",EDGE,{"derivedFrom":sQuery(id+"F0.wireOp",EDGE,"E202")}),1.0]])]});
            var Q8;
            Q8=makeQuery(id+"F0.imprint","IMPRINT",FACE,{"disambiguationData":[TD([[makeQuery(id+"F0.imprint","IMPRINT",EDGE,{"derivedFrom":sQuery(id+"F0.wireOp",EDGE,"E205")}),1.0]])]});
            var Q9;
            Q9=makeQuery(id+"F0.imprint","IMPRINT",FACE,{"disambiguationData":[TD([[makeQuery(id+"F0.imprint","IMPRINT",EDGE,{"derivedFrom":sQuery(id+"F0.wireOp",EDGE,"E207")}),1.0]])]});
            var Q10;
            Q10=makeQuery(id+"F0.imprint","IMPRINT",FACE,{"disambiguationData":[TD([[makeQuery(id+"F0.imprint","IMPRINT",EDGE,{"derivedFrom":sQuery(id+"F0.wireOp",EDGE,"E209")}),-1.0]])]});
            var Q11;
            Q11=makeQuery(id+"F0.imprint","IMPRINT",FACE,{"disambiguationData":[TD([[makeQuery(id+"F0.imprint","IMPRINT",EDGE,{"derivedFrom":sQuery(id+"F0.wireOp",EDGE,"E97")}),1.0]])]});
            var Q12;
            Q12=makeQuery(id+"F0.imprint","IMPRINT",FACE,{"disambiguationData":[TD([[makeQuery(id+"F0.imprint","IMPRINT",EDGE,{"derivedFrom":sQuery(id+"F0.wireOp",EDGE,"E111")}),-1.0]])]});
            var Q13;
            Q13=makeQuery(id+"F0.imprint","IMPRINT",FACE,{"disambiguationData":[TD([[makeQuery(id+"F0.imprint","IMPRINT",EDGE,{"derivedFrom":sQuery(id+"F0.wireOp",EDGE,"E0")}),1.0]])]});
            var Q14;
            Q14=makeQuery(id+"F0.imprint","IMPRINT",FACE,{"disambiguationData":[TD([[makeQuery(id+"F0.imprint","IMPRINT",EDGE,{"derivedFrom":sQuery(id+"F0.wireOp",EDGE,"E42")}),1.0]])]});
            var Q15;
            Q15=makeQuery(id+"F0.imprint","IMPRINT",FACE,{"disambiguationData":[TD([[makeQuery(id+"F0.imprint","IMPRINT",EDGE,{"derivedFrom":sQuery(id+"F0.wireOp",EDGE,"E82")}),-1.0]])]});
            var Q16;
            Q16=makeQuery(id+"F0.imprint","IMPRINT",FACE,{"disambiguationData":[TD([[makeQuery(id+"F0.imprint","IMPRINT",EDGE,{"derivedFrom":sQuery(id+"F0.wireOp",EDGE,"E85")}),-1.0]])]});
            var Q17;
            Q17=makeQuery(id+"F0.imprint","IMPRINT",FACE,{"disambiguationData":[TD([[makeQuery(id+"F0.imprint","IMPRINT",EDGE,{"derivedFrom":sQuery(id+"F0.wireOp",EDGE,"E88")}),1.0]])]});
            var Q18;
            Q18=makeQuery(id+"F0.imprint","IMPRINT",FACE,{"disambiguationData":[TD([[makeQuery(id+"F0.imprint","IMPRINT",EDGE,{"derivedFrom":sQuery(id+"F0.wireOp",EDGE,"E91")}),-1.0]])]});
            var Q19;
            Q19=makeQuery(id+"F0.imprint","IMPRINT",FACE,{"disambiguationData":[TD([[makeQuery(id+"F0.imprint","IMPRINT",EDGE,{"derivedFrom":sQuery(id+"F0.wireOp",EDGE,"E94")}),-1.0]])]});
            extrude(context, id + "F1", {"entities" : qUnion([Q0, Q1, Q2, Q3, Q4, Q5, Q6, Q7, Q8, Q9, Q10, Q11, Q12, Q13, Q14, Q15, Q16, Q17, Q18, Q19]), "oppositeDirection" : true, "depth" : 1.52 * mm});
        }
        {
            var Q0;
            Q0=makeQuery(id+"F0.imprint","IMPRINT",FACE,{"disambiguationData":[TD([[makeQuery(id+"F0.imprint","IMPRINT",EDGE,{"derivedFrom":sQuery(id+"F0.wireOp",EDGE,"E0")}),-1.0]])]});
            var Q1;
            Q1=makeQuery(id+"F0.imprint","IMPRINT",FACE,{"disambiguationData":[TD([[makeQuery(id+"F0.imprint","IMPRINT",EDGE,{"derivedFrom":sQuery(id+"F0.wireOp",EDGE,"E57")}),1.0]])]});
            var Q2;
            Q2=makeQuery(id+"F0.imprint","IMPRINT",FACE,{"disambiguationData":[TD([[makeQuery(id+"F0.imprint","IMPRINT",EDGE,{"derivedFrom":sQuery(id+"F0.wireOp",EDGE,"E97")}),1.0]])]});
            var Q3;
            Q3=makeQuery(id+"F0.imprint","IMPRINT",FACE,{"disambiguationData":[TD([[makeQuery(id+"F0.imprint","IMPRINT",EDGE,{"derivedFrom":sQuery(id+"F0.wireOp",EDGE,"E42")}),1.0]])]});
            var Q4;
            Q4=makeQuery(id+"F0.imprint","IMPRINT",FACE,{"disambiguationData":[TD([[makeQuery(id+"F0.imprint","IMPRINT",EDGE,{"derivedFrom":sQuery(id+"F0.wireOp",EDGE,"E111")}),-1.0]])]});
            extrude(context, id + "F2", {"entities" : qUnion([Q0, Q1, Q2, Q3, Q4]), "depth" : 0.5 * mm});
        }
        {
            var Q0;
            Q0=makeQuery(id+"F0.imprint","IMPRINT",FACE,{"disambiguationData":[TD([[makeQuery(id+"F0.imprint","IMPRINT",EDGE,{"derivedFrom":sQuery(id+"F0.wireOp",EDGE,"E0")}),1.0]])]});
            var Q1;
            Q1=makeQuery(id+"F0.imprint","IMPRINT",FACE,{"disambiguationData":[TD([[makeQuery(id+"F0.imprint","IMPRINT",EDGE,{"derivedFrom":sQuery(id+"F0.wireOp",EDGE,"E88")}),1.0]])]});
            var Q2;
            Q2=makeQuery(id+"F0.imprint","IMPRINT",FACE,{"disambiguationData":[TD([[makeQuery(id+"F0.imprint","IMPRINT",EDGE,{"derivedFrom":sQuery(id+"F0.wireOp",EDGE,"E94")}),-1.0]])]});
            var Q3;
            Q3=makeQuery(id+"F0.imprint","IMPRINT",FACE,{"disambiguationData":[TD([[makeQuery(id+"F0.imprint","IMPRINT",EDGE,{"derivedFrom":sQuery(id+"F0.wireOp",EDGE,"E91")}),-1.0]])]});
            var Q4;
            Q4=makeQuery(id+"F0.imprint","IMPRINT",FACE,{"disambiguationData":[TD([[makeQuery(id+"F0.imprint","IMPRINT",EDGE,{"derivedFrom":sQuery(id+"F0.wireOp",EDGE,"E82")}),-1.0]])]});
            var Q5;
            Q5=makeQuery(id+"F0.imprint","IMPRINT",FACE,{"disambiguationData":[TD([[makeQuery(id+"F0.imprint","IMPRINT",EDGE,{"derivedFrom":sQuery(id+"F0.wireOp",EDGE,"E192")}),1.0]])]});
            var Q6;
            Q6=makeQuery(id+"F0.imprint","IMPRINT",FACE,{"disambiguationData":[TD([[makeQuery(id+"F0.imprint","IMPRINT",EDGE,{"derivedFrom":sQuery(id+"F0.wireOp",EDGE,"E200")}),1.0]])]});
            var Q7;
            Q7=makeQuery(id+"F0.imprint","IMPRINT",FACE,{"disambiguationData":[TD([[makeQuery(id+"F0.imprint","IMPRINT",EDGE,{"derivedFrom":sQuery(id+"F0.wireOp",EDGE,"E202")}),1.0]])]});
            var Q8;
            Q8=makeQuery(id+"F0.imprint","IMPRINT",FACE,{"disambiguationData":[TD([[makeQuery(id+"F0.imprint","IMPRINT",EDGE,{"derivedFrom":sQuery(id+"F0.wireOp",EDGE,"E205")}),1.0]])]});
            var Q9;
            Q9=makeQuery(id+"F0.imprint","IMPRINT",FACE,{"disambiguationData":[TD([[makeQuery(id+"F0.imprint","IMPRINT",EDGE,{"derivedFrom":sQuery(id+"F0.wireOp",EDGE,"E207")}),1.0]])]});
            var Q10;
            Q10=makeQuery(id+"F0.imprint","IMPRINT",FACE,{"disambiguationData":[TD([[makeQuery(id+"F0.imprint","IMPRINT",EDGE,{"derivedFrom":sQuery(id+"F0.wireOp",EDGE,"E209")}),-1.0]])]});
            var Q11;
            Q11=makeQuery(id+"F0.imprint","IMPRINT",FACE,{"disambiguationData":[TD([[makeQuery(id+"F0.imprint","IMPRINT",EDGE,{"derivedFrom":sQuery(id+"F0.wireOp",EDGE,"E193")}),1.0]])]});
            extrude(context, id + "F3", {"entities" : qUnion([Q0, Q1, Q2, Q3, Q4, Q5, Q6, Q7, Q8, Q9, Q10, Q11]), "depth" : 0.5 * mm});
        }
        {
            var Q0;
            Q0=makeQuery(id+"F1.opExtrude","SWEPT_BODY",BODY,{"disambiguationData":[OSD([sQuery(id+"F0.wireOp",EDGE,"E46"),sQuery(id+"F0.wireOp",EDGE,"E47"),sQuery(id+"F0.wireOp",EDGE,"E48"),sQuery(id+"F0.wireOp",EDGE,"E49"),sQuery(id+"F0.wireOp",EDGE,"E50"),sQuery(id+"F0.wireOp",EDGE,"E51"),sQuery(id+"F0.wireOp",EDGE,"E52"),sQuery(id+"F0.wireOp",EDGE,"E53"),sQuery(id+"F0.wireOp",EDGE,"E54"),sQuery(id+"F0.wireOp",EDGE,"E55"),sQuery(id+"F0.wireOp",EDGE,"E56"),sQuery(id+"F0.wireOp",EDGE,"E120"),sQuery(id+"F0.wireOp",EDGE,"E121"),sQuery(id+"F0.wireOp",EDGE,"E122"),sQuery(id+"F0.wireOp",EDGE,"E123"),sQuery(id+"F0.wireOp",EDGE,"E124"),sQuery(id+"F0.wireOp",EDGE,"E125"),sQuery(id+"F0.wireOp",EDGE,"E126"),sQuery(id+"F0.wireOp",EDGE,"E127"),sQuery(id+"F0.wireOp",EDGE,"E242"),sQuery(id+"F0.wireOp",EDGE,"E243"),sQuery(id+"F0.wireOp",EDGE,"E244"),sQuery(id+"F0.wireOp",EDGE,"E245"),sQuery(id+"F0.wireOp",EDGE,"E246"),sQuery(id+"F0.wireOp",EDGE,"E247"),sQuery(id+"F0.wireOp",EDGE,"E248"),sQuery(id+"F0.wireOp",EDGE,"E249"),sQuery(id+"F0.wireOp",EDGE,"E250"),sQuery(id+"F0.wireOp",EDGE,"E251"),sQuery(id+"F0.wireOp",EDGE,"E252"),sQuery(id+"F0.wireOp",EDGE,"E253"),sQuery(id+"F0.wireOp",EDGE,"E254"),sQuery(id+"F0.wireOp",EDGE,"E255"),sQuery(id+"F0.wireOp",EDGE,"E256"),sQuery(id+"F0.wireOp",EDGE,"E257"),sQuery(id+"F0.wireOp",EDGE,"E258"),sQuery(id+"F0.wireOp",EDGE,"E259"),sQuery(id+"F0.wireOp",EDGE,"E260"),sQuery(id+"F0.wireOp",EDGE,"E261"),sQuery(id+"F0.wireOp",EDGE,"E262"),sQuery(id+"F0.wireOp",EDGE,"E263"),sQuery(id+"F0.wireOp",EDGE,"E264"),sQuery(id+"F0.wireOp",EDGE,"E265"),sQuery(id+"F0.wireOp",EDGE,"E266"),sQuery(id+"F0.wireOp",EDGE,"E267"),sQuery(id+"F0.wireOp",EDGE,"E268"),sQuery(id+"F0.wireOp",EDGE,"E269"),sQuery(id+"F0.wireOp",EDGE,"E270"),sQuery(id+"F0.wireOp",EDGE,"E271")])]});
            var Q1;
            Q1=makeQuery(id+"F2.opExtrude","SWEPT_BODY",BODY,{"disambiguationData":[OSD([sQuery(id+"F0.wireOp",EDGE,"E0"),sQuery(id+"F0.wireOp",EDGE,"E1"),sQuery(id+"F0.wireOp",EDGE,"E2"),sQuery(id+"F0.wireOp",EDGE,"E3"),sQuery(id+"F0.wireOp",EDGE,"E4"),sQuery(id+"F0.wireOp",EDGE,"E5"),sQuery(id+"F0.wireOp",EDGE,"E6"),sQuery(id+"F0.wireOp",EDGE,"E7"),sQuery(id+"F0.wireOp",EDGE,"E8"),sQuery(id+"F0.wireOp",EDGE,"E9"),sQuery(id+"F0.wireOp",EDGE,"E10"),sQuery(id+"F0.wireOp",EDGE,"E11"),sQuery(id+"F0.wireOp",EDGE,"E12"),sQuery(id+"F0.wireOp",EDGE,"E13"),sQuery(id+"F0.wireOp",EDGE,"E14"),sQuery(id+"F0.wireOp",EDGE,"E15"),sQuery(id+"F0.wireOp",EDGE,"E16"),sQuery(id+"F0.wireOp",EDGE,"E17"),sQuery(id+"F0.wireOp",EDGE,"E18"),sQuery(id+"F0.wireOp",EDGE,"E19"),sQuery(id+"F0.wireOp",EDGE,"E20"),sQuery(id+"F0.wireOp",EDGE,"E21"),sQuery(id+"F0.wireOp",EDGE,"E22"),sQuery(id+"F0.wireOp",EDGE,"E23"),sQuery(id+"F0.wireOp",EDGE,"E24"),sQuery(id+"F0.wireOp",EDGE,"E25"),sQuery(id+"F0.wireOp",EDGE,"E26"),sQuery(id+"F0.wireOp",EDGE,"E27"),sQuery(id+"F0.wireOp",EDGE,"E28"),sQuery(id+"F0.wireOp",EDGE,"E29"),sQuery(id+"F0.wireOp",EDGE,"E30"),sQuery(id+"F0.wireOp",EDGE,"E31"),sQuery(id+"F0.wireOp",EDGE,"E32"),sQuery(id+"F0.wireOp",EDGE,"E33"),sQuery(id+"F0.wireOp",EDGE,"E34"),sQuery(id+"F0.wireOp",EDGE,"E35"),sQuery(id+"F0.wireOp",EDGE,"E36"),sQuery(id+"F0.wireOp",EDGE,"E37"),sQuery(id+"F0.wireOp",EDGE,"E38"),sQuery(id+"F0.wireOp",EDGE,"E39"),sQuery(id+"F0.wireOp",EDGE,"E40"),sQuery(id+"F0.wireOp",EDGE,"E41")])]});
            var Q2;
            Q2=makeQuery(id+"F2.opExtrude","SWEPT_BODY",BODY,{"disambiguationData":[OSD([sQuery(id+"F0.wireOp",EDGE,"E42"),sQuery(id+"F0.wireOp",EDGE,"E43"),sQuery(id+"F0.wireOp",EDGE,"E44"),sQuery(id+"F0.wireOp",EDGE,"E45")])]});
            var Q3;
            Q3=makeQuery(id+"F2.opExtrude","SWEPT_BODY",BODY,{"disambiguationData":[OSD([sQuery(id+"F0.wireOp",EDGE,"E57"),sQuery(id+"F0.wireOp",EDGE,"E58"),sQuery(id+"F0.wireOp",EDGE,"E59"),sQuery(id+"F0.wireOp",EDGE,"E60"),sQuery(id+"F0.wireOp",EDGE,"E61"),sQuery(id+"F0.wireOp",EDGE,"E62"),sQuery(id+"F0.wireOp",EDGE,"E63"),sQuery(id+"F0.wireOp",EDGE,"E64"),sQuery(id+"F0.wireOp",EDGE,"E65"),sQuery(id+"F0.wireOp",EDGE,"E66"),sQuery(id+"F0.wireOp",EDGE,"E67"),sQuery(id+"F0.wireOp",EDGE,"E68"),sQuery(id+"F0.wireOp",EDGE,"E69"),sQuery(id+"F0.wireOp",EDGE,"E70"),sQuery(id+"F0.wireOp",EDGE,"E71"),sQuery(id+"F0.wireOp",EDGE,"E72"),sQuery(id+"F0.wireOp",EDGE,"E73"),sQuery(id+"F0.wireOp",EDGE,"E74"),sQuery(id+"F0.wireOp",EDGE,"E75"),sQuery(id+"F0.wireOp",EDGE,"E76"),sQuery(id+"F0.wireOp",EDGE,"E77"),sQuery(id+"F0.wireOp",EDGE,"E78"),sQuery(id+"F0.wireOp",EDGE,"E79"),sQuery(id+"F0.wireOp",EDGE,"E80"),sQuery(id+"F0.wireOp",EDGE,"E81"),sQuery(id+"F0.wireOp",EDGE,"E82"),sQuery(id+"F0.wireOp",EDGE,"E83"),sQuery(id+"F0.wireOp",EDGE,"E84"),sQuery(id+"F0.wireOp",EDGE,"E85"),sQuery(id+"F0.wireOp",EDGE,"E86"),sQuery(id+"F0.wireOp",EDGE,"E87"),sQuery(id+"F0.wireOp",EDGE,"E88"),sQuery(id+"F0.wireOp",EDGE,"E89"),sQuery(id+"F0.wireOp",EDGE,"E90"),sQuery(id+"F0.wireOp",EDGE,"E91"),sQuery(id+"F0.wireOp",EDGE,"E92"),sQuery(id+"F0.wireOp",EDGE,"E93"),sQuery(id+"F0.wireOp",EDGE,"E94"),sQuery(id+"F0.wireOp",EDGE,"E95"),sQuery(id+"F0.wireOp",EDGE,"E96")])]});
            var Q4;
            Q4=makeQuery(id+"F2.opExtrude","SWEPT_BODY",BODY,{"disambiguationData":[OSD([sQuery(id+"F0.wireOp",EDGE,"E97"),sQuery(id+"F0.wireOp",EDGE,"E98"),sQuery(id+"F0.wireOp",EDGE,"E99"),sQuery(id+"F0.wireOp",EDGE,"E100"),sQuery(id+"F0.wireOp",EDGE,"E101"),sQuery(id+"F0.wireOp",EDGE,"E102"),sQuery(id+"F0.wireOp",EDGE,"E103"),sQuery(id+"F0.wireOp",EDGE,"E104"),sQuery(id+"F0.wireOp",EDGE,"E105"),sQuery(id+"F0.wireOp",EDGE,"E106"),sQuery(id+"F0.wireOp",EDGE,"E107"),sQuery(id+"F0.wireOp",EDGE,"E108"),sQuery(id+"F0.wireOp",EDGE,"E109"),sQuery(id+"F0.wireOp",EDGE,"E110")])]});
            var Q5;
            Q5=makeQuery(id+"F2.opExtrude","SWEPT_BODY",BODY,{"disambiguationData":[OSD([sQuery(id+"F0.wireOp",EDGE,"E111"),sQuery(id+"F0.wireOp",EDGE,"E112"),sQuery(id+"F0.wireOp",EDGE,"E113"),sQuery(id+"F0.wireOp",EDGE,"E114"),sQuery(id+"F0.wireOp",EDGE,"E115"),sQuery(id+"F0.wireOp",EDGE,"E116"),sQuery(id+"F0.wireOp",EDGE,"E117"),sQuery(id+"F0.wireOp",EDGE,"E118"),sQuery(id+"F0.wireOp",EDGE,"E119")])]});
            var Q6;
            Q6=makeQuery(id+"F3.opExtrude","SWEPT_BODY",BODY,{"disambiguationData":[OSD([sQuery(id+"F0.wireOp",EDGE,"E0"),sQuery(id+"F0.wireOp",EDGE,"E1"),sQuery(id+"F0.wireOp",EDGE,"E2"),sQuery(id+"F0.wireOp",EDGE,"E3"),sQuery(id+"F0.wireOp",EDGE,"E4"),sQuery(id+"F0.wireOp",EDGE,"E5"),sQuery(id+"F0.wireOp",EDGE,"E6"),sQuery(id+"F0.wireOp",EDGE,"E7"),sQuery(id+"F0.wireOp",EDGE,"E8"),sQuery(id+"F0.wireOp",EDGE,"E9"),sQuery(id+"F0.wireOp",EDGE,"E10"),sQuery(id+"F0.wireOp",EDGE,"E11"),sQuery(id+"F0.wireOp",EDGE,"E12"),sQuery(id+"F0.wireOp",EDGE,"E13"),sQuery(id+"F0.wireOp",EDGE,"E14"),sQuery(id+"F0.wireOp",EDGE,"E15"),sQuery(id+"F0.wireOp",EDGE,"E16"),sQuery(id+"F0.wireOp",EDGE,"E17"),sQuery(id+"F0.wireOp",EDGE,"E18"),sQuery(id+"F0.wireOp",EDGE,"E19"),sQuery(id+"F0.wireOp",EDGE,"E20"),sQuery(id+"F0.wireOp",EDGE,"E21"),sQuery(id+"F0.wireOp",EDGE,"E22"),sQuery(id+"F0.wireOp",EDGE,"E23"),sQuery(id+"F0.wireOp",EDGE,"E24"),sQuery(id+"F0.wireOp",EDGE,"E25"),sQuery(id+"F0.wireOp",EDGE,"E26"),sQuery(id+"F0.wireOp",EDGE,"E27"),sQuery(id+"F0.wireOp",EDGE,"E28"),sQuery(id+"F0.wireOp",EDGE,"E29"),sQuery(id+"F0.wireOp",EDGE,"E30"),sQuery(id+"F0.wireOp",EDGE,"E31"),sQuery(id+"F0.wireOp",EDGE,"E32"),sQuery(id+"F0.wireOp",EDGE,"E33"),sQuery(id+"F0.wireOp",EDGE,"E34"),sQuery(id+"F0.wireOp",EDGE,"E35"),sQuery(id+"F0.wireOp",EDGE,"E36"),sQuery(id+"F0.wireOp",EDGE,"E37"),sQuery(id+"F0.wireOp",EDGE,"E38"),sQuery(id+"F0.wireOp",EDGE,"E39"),sQuery(id+"F0.wireOp",EDGE,"E40"),sQuery(id+"F0.wireOp",EDGE,"E41"),sQuery(id+"F0.wireOp",EDGE,"E42"),sQuery(id+"F0.wireOp",EDGE,"E43"),sQuery(id+"F0.wireOp",EDGE,"E44"),sQuery(id+"F0.wireOp",EDGE,"E45"),sQuery(id+"F0.wireOp",EDGE,"E46"),sQuery(id+"F0.wireOp",EDGE,"E47"),sQuery(id+"F0.wireOp",EDGE,"E48"),sQuery(id+"F0.wireOp",EDGE,"E49"),sQuery(id+"F0.wireOp",EDGE,"E50"),sQuery(id+"F0.wireOp",EDGE,"E51"),sQuery(id+"F0.wireOp",EDGE,"E52"),sQuery(id+"F0.wireOp",EDGE,"E53"),sQuery(id+"F0.wireOp",EDGE,"E54"),sQuery(id+"F0.wireOp",EDGE,"E55"),sQuery(id+"F0.wireOp",EDGE,"E56"),sQuery(id+"F0.wireOp",EDGE,"E57"),sQuery(id+"F0.wireOp",EDGE,"E58"),sQuery(id+"F0.wireOp",EDGE,"E59"),sQuery(id+"F0.wireOp",EDGE,"E60"),sQuery(id+"F0.wireOp",EDGE,"E61"),sQuery(id+"F0.wireOp",EDGE,"E62"),sQuery(id+"F0.wireOp",EDGE,"E63"),sQuery(id+"F0.wireOp",EDGE,"E64"),sQuery(id+"F0.wireOp",EDGE,"E65"),sQuery(id+"F0.wireOp",EDGE,"E66"),sQuery(id+"F0.wireOp",EDGE,"E67"),sQuery(id+"F0.wireOp",EDGE,"E68"),sQuery(id+"F0.wireOp",EDGE,"E69"),sQuery(id+"F0.wireOp",EDGE,"E70"),sQuery(id+"F0.wireOp",EDGE,"E71"),sQuery(id+"F0.wireOp",EDGE,"E72"),sQuery(id+"F0.wireOp",EDGE,"E73"),sQuery(id+"F0.wireOp",EDGE,"E74"),sQuery(id+"F0.wireOp",EDGE,"E75"),sQuery(id+"F0.wireOp",EDGE,"E76"),sQuery(id+"F0.wireOp",EDGE,"E77"),sQuery(id+"F0.wireOp",EDGE,"E78"),sQuery(id+"F0.wireOp",EDGE,"E79"),sQuery(id+"F0.wireOp",EDGE,"E80"),sQuery(id+"F0.wireOp",EDGE,"E81"),sQuery(id+"F0.wireOp",EDGE,"E97"),sQuery(id+"F0.wireOp",EDGE,"E98"),sQuery(id+"F0.wireOp",EDGE,"E99"),sQuery(id+"F0.wireOp",EDGE,"E100"),sQuery(id+"F0.wireOp",EDGE,"E101"),sQuery(id+"F0.wireOp",EDGE,"E102"),sQuery(id+"F0.wireOp",EDGE,"E103"),sQuery(id+"F0.wireOp",EDGE,"E104"),sQuery(id+"F0.wireOp",EDGE,"E105"),sQuery(id+"F0.wireOp",EDGE,"E106"),sQuery(id+"F0.wireOp",EDGE,"E107"),sQuery(id+"F0.wireOp",EDGE,"E108"),sQuery(id+"F0.wireOp",EDGE,"E109"),sQuery(id+"F0.wireOp",EDGE,"E110"),sQuery(id+"F0.wireOp",EDGE,"E111"),sQuery(id+"F0.wireOp",EDGE,"E112"),sQuery(id+"F0.wireOp",EDGE,"E113"),sQuery(id+"F0.wireOp",EDGE,"E114"),sQuery(id+"F0.wireOp",EDGE,"E115"),sQuery(id+"F0.wireOp",EDGE,"E116"),sQuery(id+"F0.wireOp",EDGE,"E117"),sQuery(id+"F0.wireOp",EDGE,"E118"),sQuery(id+"F0.wireOp",EDGE,"E119"),sQuery(id+"F0.wireOp",EDGE,"E120"),sQuery(id+"F0.wireOp",EDGE,"E121"),sQuery(id+"F0.wireOp",EDGE,"E122"),sQuery(id+"F0.wireOp",EDGE,"E123"),sQuery(id+"F0.wireOp",EDGE,"E124"),sQuery(id+"F0.wireOp",EDGE,"E125"),sQuery(id+"F0.wireOp",EDGE,"E126"),sQuery(id+"F0.wireOp",EDGE,"E127"),sQuery(id+"F0.wireOp",EDGE,"E128"),sQuery(id+"F0.wireOp",EDGE,"E129"),sQuery(id+"F0.wireOp",EDGE,"E130"),sQuery(id+"F0.wireOp",EDGE,"E131"),sQuery(id+"F0.wireOp",EDGE,"E132"),sQuery(id+"F0.wireOp",EDGE,"E133"),sQuery(id+"F0.wireOp",EDGE,"E134"),sQuery(id+"F0.wireOp",EDGE,"E135"),sQuery(id+"F0.wireOp",EDGE,"E136"),sQuery(id+"F0.wireOp",EDGE,"E137"),sQuery(id+"F0.wireOp",EDGE,"E138"),sQuery(id+"F0.wireOp",EDGE,"E139"),sQuery(id+"F0.wireOp",EDGE,"E140"),sQuery(id+"F0.wireOp",EDGE,"E141"),sQuery(id+"F0.wireOp",EDGE,"E142"),sQuery(id+"F0.wireOp",EDGE,"E143"),sQuery(id+"F0.wireOp",EDGE,"E144"),sQuery(id+"F0.wireOp",EDGE,"E145"),sQuery(id+"F0.wireOp",EDGE,"E146"),sQuery(id+"F0.wireOp",EDGE,"E147"),sQuery(id+"F0.wireOp",EDGE,"E148"),sQuery(id+"F0.wireOp",EDGE,"E149"),sQuery(id+"F0.wireOp",EDGE,"E150"),sQuery(id+"F0.wireOp",EDGE,"E151"),sQuery(id+"F0.wireOp",EDGE,"E152"),sQuery(id+"F0.wireOp",EDGE,"E153"),sQuery(id+"F0.wireOp",EDGE,"E154"),sQuery(id+"F0.wireOp",EDGE,"E155"),sQuery(id+"F0.wireOp",EDGE,"E156"),sQuery(id+"F0.wireOp",EDGE,"E157"),sQuery(id+"F0.wireOp",EDGE,"E158"),sQuery(id+"F0.wireOp",EDGE,"E159"),sQuery(id+"F0.wireOp",EDGE,"E161"),sQuery(id+"F0.wireOp",EDGE,"E162"),sQuery(id+"F0.wireOp",EDGE,"E163"),sQuery(id+"F0.wireOp",EDGE,"E164"),sQuery(id+"F0.wireOp",EDGE,"E165"),sQuery(id+"F0.wireOp",EDGE,"E166"),sQuery(id+"F0.wireOp",EDGE,"E167"),sQuery(id+"F0.wireOp",EDGE,"E168"),sQuery(id+"F0.wireOp",EDGE,"E169"),sQuery(id+"F0.wireOp",EDGE,"E170"),sQuery(id+"F0.wireOp",EDGE,"E171"),sQuery(id+"F0.wireOp",EDGE,"E172"),sQuery(id+"F0.wireOp",EDGE,"E173"),sQuery(id+"F0.wireOp",EDGE,"E174"),sQuery(id+"F0.wireOp",EDGE,"E175"),sQuery(id+"F0.wireOp",EDGE,"E176"),sQuery(id+"F0.wireOp",EDGE,"E177"),sQuery(id+"F0.wireOp",EDGE,"E178"),sQuery(id+"F0.wireOp",EDGE,"E179"),sQuery(id+"F0.wireOp",EDGE,"E180"),sQuery(id+"F0.wireOp",EDGE,"E181"),sQuery(id+"F0.wireOp",EDGE,"E182"),sQuery(id+"F0.wireOp",EDGE,"E183"),sQuery(id+"F0.wireOp",EDGE,"E184"),sQuery(id+"F0.wireOp",EDGE,"E185"),sQuery(id+"F0.wireOp",EDGE,"E186"),sQuery(id+"F0.wireOp",EDGE,"E187"),sQuery(id+"F0.wireOp",EDGE,"E188"),sQuery(id+"F0.wireOp",EDGE,"E189"),sQuery(id+"F0.wireOp",EDGE,"E190"),sQuery(id+"F0.wireOp",EDGE,"E191"),sQuery(id+"F0.wireOp",EDGE,"E212"),sQuery(id+"F0.wireOp",EDGE,"E213"),sQuery(id+"F0.wireOp",EDGE,"E214"),sQuery(id+"F0.wireOp",EDGE,"E215"),sQuery(id+"F0.wireOp",EDGE,"E216"),sQuery(id+"F0.wireOp",EDGE,"E217"),sQuery(id+"F0.wireOp",EDGE,"E218"),sQuery(id+"F0.wireOp",EDGE,"E219"),sQuery(id+"F0.wireOp",EDGE,"E220"),sQuery(id+"F0.wireOp",EDGE,"E221"),sQuery(id+"F0.wireOp",EDGE,"E222"),sQuery(id+"F0.wireOp",EDGE,"E223"),sQuery(id+"F0.wireOp",EDGE,"E224"),sQuery(id+"F0.wireOp",EDGE,"E225"),sQuery(id+"F0.wireOp",EDGE,"E226"),sQuery(id+"F0.wireOp",EDGE,"E227"),sQuery(id+"F0.wireOp",EDGE,"E228"),sQuery(id+"F0.wireOp",EDGE,"E229"),sQuery(id+"F0.wireOp",EDGE,"E230"),sQuery(id+"F0.wireOp",EDGE,"E231"),sQuery(id+"F0.wireOp",EDGE,"E232"),sQuery(id+"F0.wireOp",EDGE,"E233"),sQuery(id+"F0.wireOp",EDGE,"E234"),sQuery(id+"F0.wireOp",EDGE,"E235"),sQuery(id+"F0.wireOp",EDGE,"E236"),sQuery(id+"F0.wireOp",EDGE,"E237"),sQuery(id+"F0.wireOp",EDGE,"E238"),sQuery(id+"F0.wireOp",EDGE,"E239"),sQuery(id+"F0.wireOp",EDGE,"E240"),sQuery(id+"F0.wireOp",EDGE,"E241")])]});
            var Q7;
            Q7=makeQuery(id+"F3.opExtrude","SWEPT_BODY",BODY,{"disambiguationData":[OSD([sQuery(id+"F0.wireOp",EDGE,"E82"),sQuery(id+"F0.wireOp",EDGE,"E83"),sQuery(id+"F0.wireOp",EDGE,"E84")])]});
            var Q8;
            Q8=makeQuery(id+"F3.opExtrude","SWEPT_BODY",BODY,{"disambiguationData":[OSD([sQuery(id+"F0.wireOp",EDGE,"E88"),sQuery(id+"F0.wireOp",EDGE,"E89"),sQuery(id+"F0.wireOp",EDGE,"E90")])]});
            var Q9;
            Q9=makeQuery(id+"F3.opExtrude","SWEPT_BODY",BODY,{"disambiguationData":[OSD([sQuery(id+"F0.wireOp",EDGE,"E91"),sQuery(id+"F0.wireOp",EDGE,"E92"),sQuery(id+"F0.wireOp",EDGE,"E93")])]});
            var Q10;
            Q10=makeQuery(id+"F3.opExtrude","SWEPT_BODY",BODY,{"disambiguationData":[OSD([sQuery(id+"F0.wireOp",EDGE,"E94"),sQuery(id+"F0.wireOp",EDGE,"E95"),sQuery(id+"F0.wireOp",EDGE,"E96")])]});
            var Q11;
            Q11=makeQuery(id+"F3.opExtrude","SWEPT_BODY",BODY,{"disambiguationData":[OSD([sQuery(id+"F0.wireOp",EDGE,"E192"),sQuery(id+"F0.wireOp",EDGE,"E197"),sQuery(id+"F0.wireOp",EDGE,"E198"),sQuery(id+"F0.wireOp",EDGE,"E199")])]});
            var Q12;
            Q12=makeQuery(id+"F3.opExtrude","SWEPT_BODY",BODY,{"disambiguationData":[OSD([sQuery(id+"F0.wireOp",EDGE,"E193"),sQuery(id+"F0.wireOp",EDGE,"E194"),sQuery(id+"F0.wireOp",EDGE,"E195"),sQuery(id+"F0.wireOp",EDGE,"E196")])]});
            var Q13;
            Q13=makeQuery(id+"F3.opExtrude","SWEPT_BODY",BODY,{"disambiguationData":[OSD([sQuery(id+"F0.wireOp",EDGE,"E200"),sQuery(id+"F0.wireOp",EDGE,"E201")])]});
            var Q14;
            Q14=makeQuery(id+"F3.opExtrude","SWEPT_BODY",BODY,{"disambiguationData":[OSD([sQuery(id+"F0.wireOp",EDGE,"E202"),sQuery(id+"F0.wireOp",EDGE,"E203"),sQuery(id+"F0.wireOp",EDGE,"E204")])]});
            var Q15;
            Q15=makeQuery(id+"F3.opExtrude","SWEPT_BODY",BODY,{"disambiguationData":[OSD([sQuery(id+"F0.wireOp",EDGE,"E205"),sQuery(id+"F0.wireOp",EDGE,"E206")])]});
            var Q16;
            Q16=makeQuery(id+"F3.opExtrude","SWEPT_BODY",BODY,{"disambiguationData":[OSD([sQuery(id+"F0.wireOp",EDGE,"E207"),sQuery(id+"F0.wireOp",EDGE,"E208")])]});
            var Q17;
            Q17=makeQuery(id+"F3.opExtrude","SWEPT_BODY",BODY,{"disambiguationData":[OSD([sQuery(id+"F0.wireOp",EDGE,"E209"),sQuery(id+"F0.wireOp",EDGE,"E210"),sQuery(id+"F0.wireOp",EDGE,"E211")])]});
            transform(context, id + "F4", {"entities" : qUnion([Q0, Q1, Q2, Q3, Q4, Q5, Q6, Q7, Q8, Q9, Q10, Q11, Q12, Q13, Q14, Q15, Q16, Q17]), "transformType" : TransformType.TRANSLATION_3D, "dx" : 0 * mm, "dy" : 0 * mm, "dz" : 1.52 * mm, "makeCopy" : false});
        }
    });
